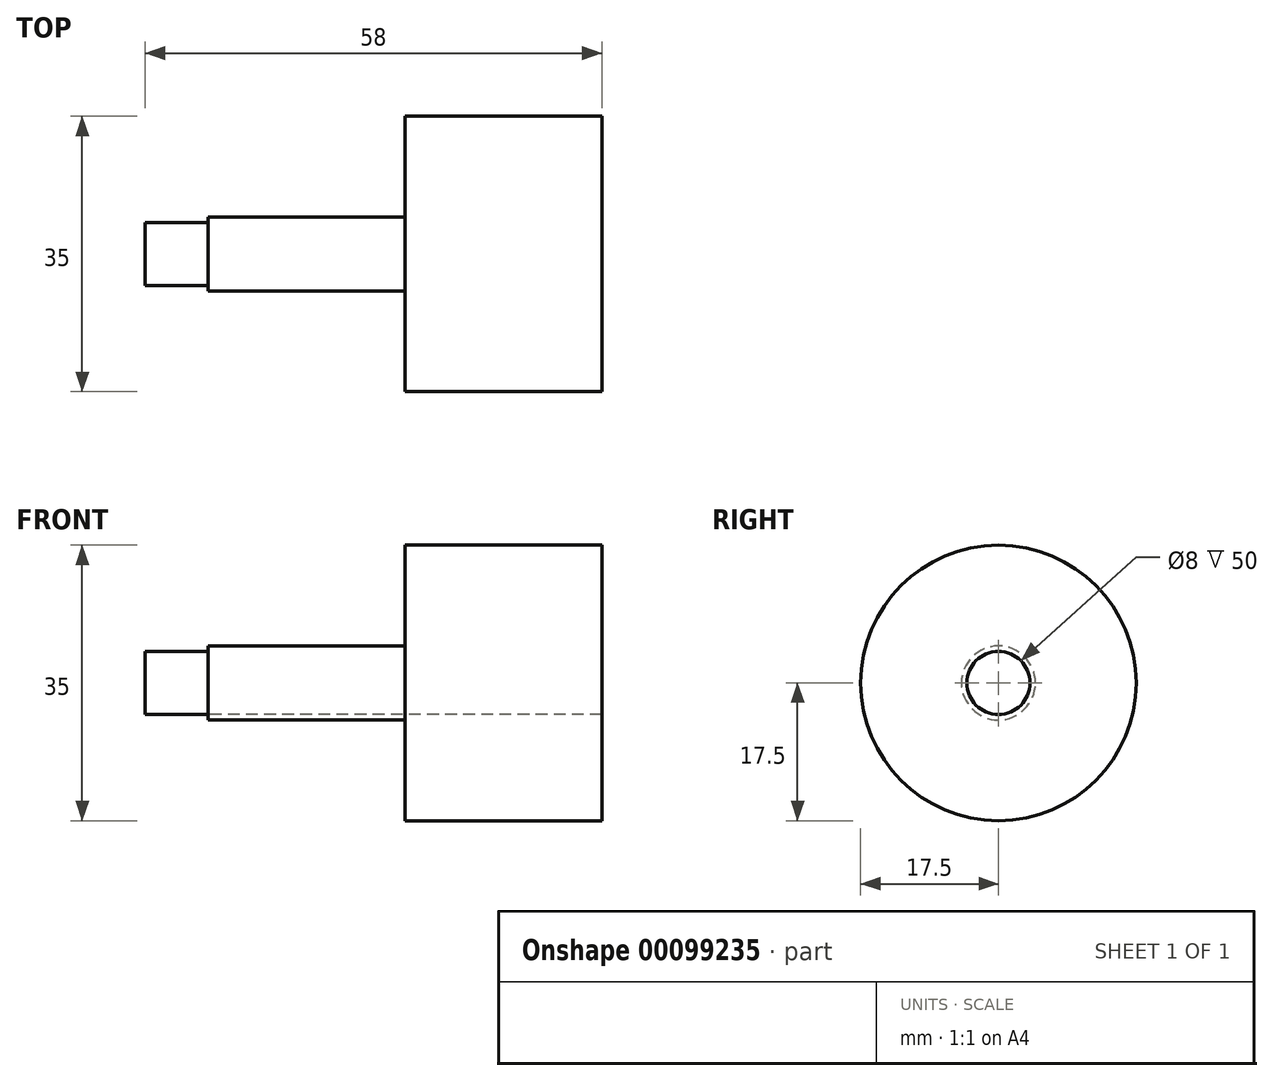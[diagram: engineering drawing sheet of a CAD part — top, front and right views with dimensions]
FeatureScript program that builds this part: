
annotation { "Feature Type Name" : "Feature", "Feature Type Description" : "" }
export const myFeature = defineFeature(function(context is Context, id is Id, definition is map)
    precondition{}
    {
        {
            var Q0;
            Q0=qCreatedBy(makeId("Right.planeOp"),FACE);
            var sketch = newSketch(context, id + "F0", { "sketchPlane" : qUnion([Q0])});
            skCircle(sketch, "E0", {"center": v(0, 0) * mm, "radius": 4 * mm});
            skSolve(sketch);
        }
        {
            var Q0;
            Q0=makeQuery(id+"F0.imprint","IMPRINT",FACE,{"disambiguationData":[TD([[makeQuery(id+"F0.imprint","IMPRINT",EDGE,{"derivedFrom":sQuery(id+"F0.wireOp",EDGE,"E0")}),1.0]])]});
            extrude(context, id + "F1", {"entities" : qUnion([Q0]), "depth" : 8 * mm});
        }
        {
            var Q0;
            Q0=makeQuery(id+"F1.opExtrude","CAP_FACE",FACE,{"disambiguationData":[OSD([sQuery(id+"F0.wireOp",EDGE,"E0")])],"isStart":false});
            var sketch = newSketch(context, id + "F2", { "sketchPlane" : qUnion([Q0])});
            skCircle(sketch, "E1", {"center": v(0, 0) * mm, "radius": 4.7 * mm});
            skSolve(sketch);
        }
        {
            var Q0;
            Q0=makeQuery(id+"F2.imprint","IMPRINT",FACE,{"disambiguationData":[TD([[makeQuery(id+"F2.imprint","IMPRINT",EDGE,{"derivedFrom":sQuery(id+"F2.wireOp",EDGE,"E1")}),1.0]])]});
            extrude(context, id + "F3", {"entities" : qUnion([Q0]), "operationType" : NewBodyOperationType.ADD, "depth" : 25 * mm});
        }
        {
            var Q0;
            Q0=makeQuery(id+"F3.opExtrude","CAP_FACE",FACE,{"disambiguationData":[OSD([sQuery(id+"F2.wireOp",EDGE,"E1")])],"isStart":false});
            var sketch = newSketch(context, id + "F4", { "sketchPlane" : qUnion([Q0])});
            skCircle(sketch, "E2", {"center": v(0, 0) * mm, "radius": 17.5 * mm});
            skSolve(sketch);
        }
        {
            var Q0;
            Q0=makeQuery(id+"F4.imprint","IMPRINT",FACE,{"disambiguationData":[TD([[makeQuery(id+"F4.imprint","IMPRINT",EDGE,{"derivedFrom":makeQuery(id+"F3.opExtrude","CAP_EDGE",EDGE,{"disambiguationData":[OSD([sQuery(id+"F2.wireOp",EDGE,"E1")])],"isStart":false})}),1.0]])]});
            var Q1;
            Q1=makeQuery(id+"F4.imprint","IMPRINT",FACE,{"disambiguationData":[TD([[makeQuery(id+"F4.imprint","IMPRINT",EDGE,{"derivedFrom":sQuery(id+"F4.wireOp",EDGE,"E2")}),1.0]])]});
            extrude(context, id + "F5", {"entities" : qUnion([Q0, Q1]), "operationType" : NewBodyOperationType.ADD, "depth" : 25 * mm});
        }
    });
